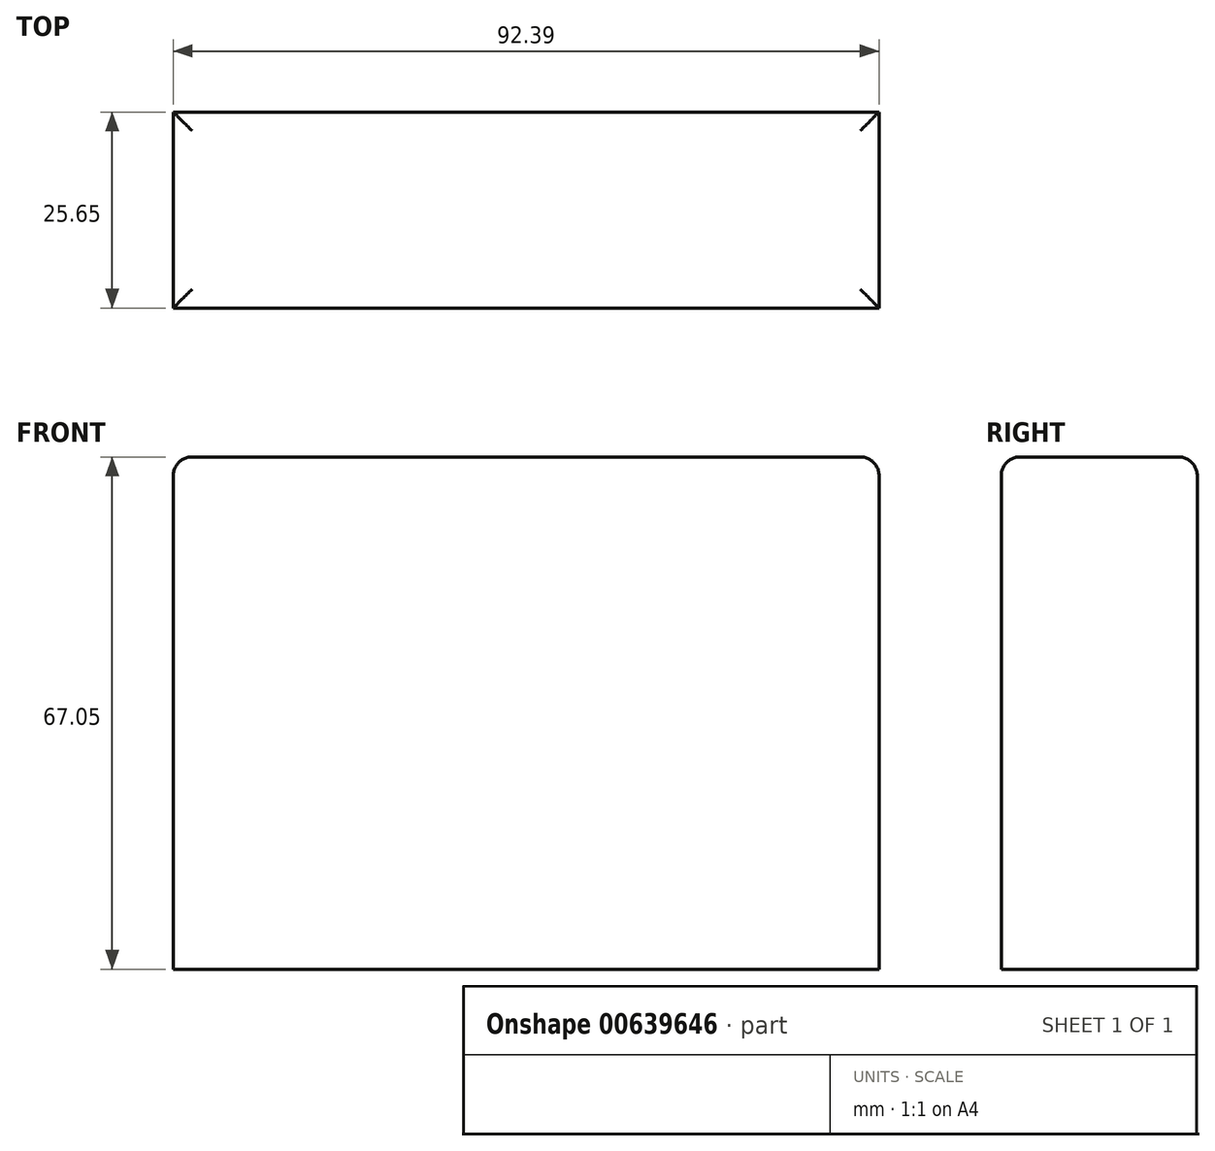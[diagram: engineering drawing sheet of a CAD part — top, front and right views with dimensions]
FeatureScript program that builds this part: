
annotation { "Feature Type Name" : "Feature", "Feature Type Description" : "" }
export const myFeature = defineFeature(function(context is Context, id is Id, definition is map)
    precondition{}
    {
        {
            var Q0;
            Q0=qCreatedBy(makeId("Front.planeOp"),FACE);
            var sketch = newSketch(context, id + "F0", { "sketchPlane" : qUnion([Q0])});
            skLineSegment(sketch, "E0.bottom", {"start": v(-41.88, 32.95) * mm, "end": v(50.5, 32.95) * mm});
            skLineSegment(sketch, "E0.top", {"start": v(-41.88, -34.1) * mm, "end": v(50.5, -34.1) * mm});
            skLineSegment(sketch, "E0.left", {"start": v(-41.88, 32.95) * mm, "end": v(-41.88, -34.1) * mm});
            skLineSegment(sketch, "E0.right", {"start": v(50.5, 32.95) * mm, "end": v(50.5, -34.1) * mm});
            skSolve(sketch);
        }
        {
            var Q0;
            Q0=makeQuery(id+"F0.imprint","IMPRINT",FACE,{"disambiguationData":[TD([[makeQuery(id+"F0.imprint","IMPRINT",EDGE,{"derivedFrom":sQuery(id+"F0.wireOp",EDGE,"E0.bottom")}),-1.0]])]});
            extrude(context, id + "F1", {"entities" : qUnion([Q0]), "depth" : 25.65 * mm, "offsetDistance" : 25.4 * mm});
        }
        {
            var Q0;
            Q0=makeQuery(id+"F1.opExtrude","SWEPT_FACE",FACE,{"disambiguationData":[OSD([sQuery(id+"F0.wireOp",EDGE,"E0.bottom")])]});
            fillet(context, id + "F2", {"entities" : qUnion([Q0]), "radius" : 2.45 * mm, "tangentPropagation" : true, "allowEdgeOverflow" : false});
        }
    });
